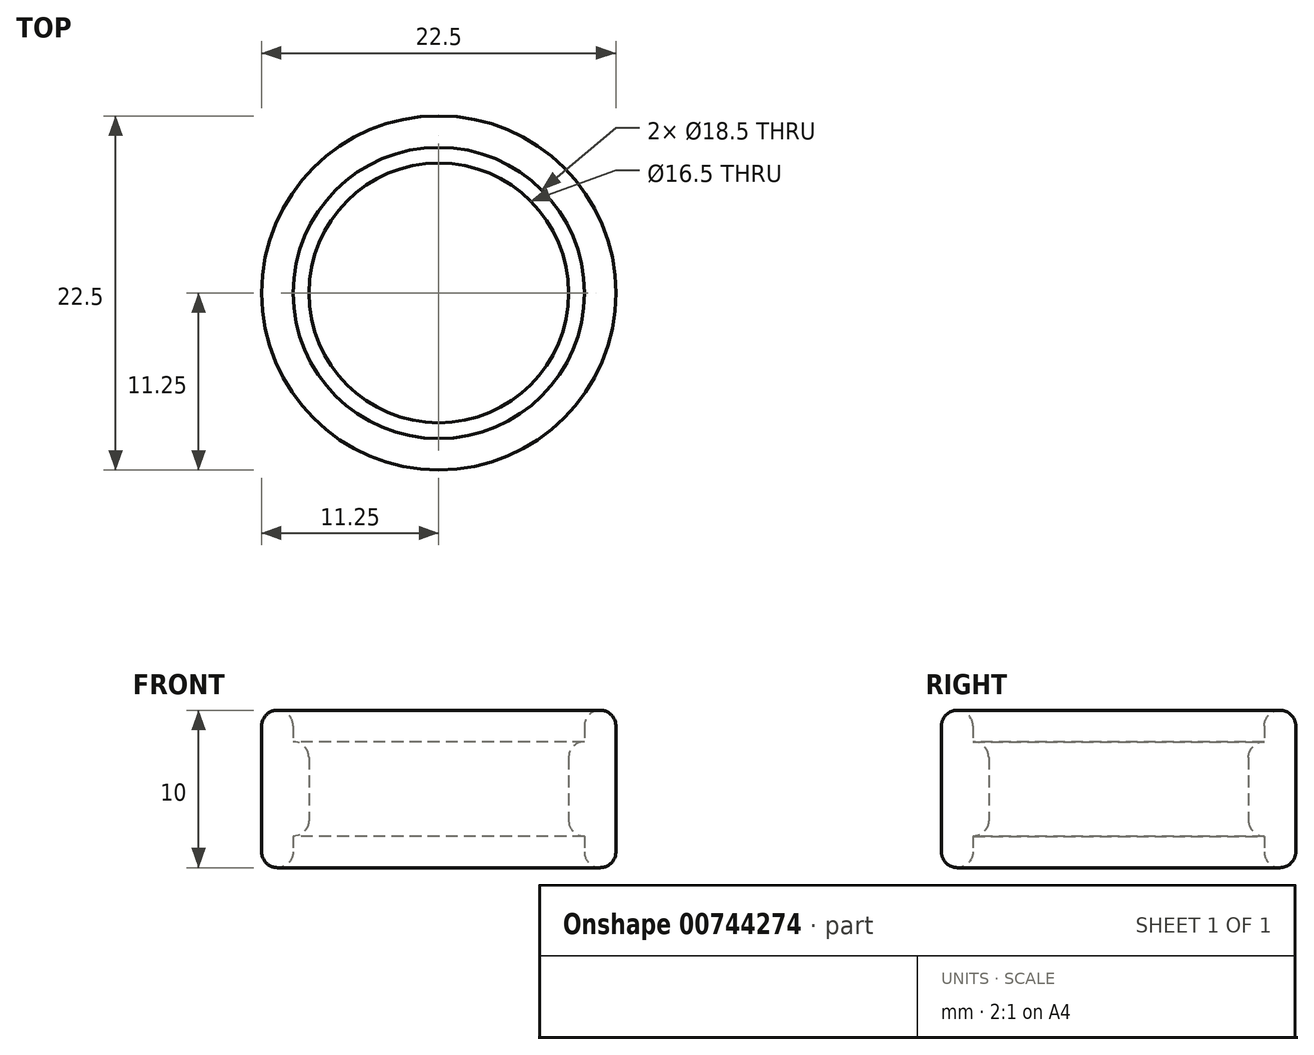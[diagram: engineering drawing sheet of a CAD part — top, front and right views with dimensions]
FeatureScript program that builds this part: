
annotation { "Feature Type Name" : "Feature", "Feature Type Description" : "" }
export const myFeature = defineFeature(function(context is Context, id is Id, definition is map)
    precondition{}
    {
        {
            var Q0;
            Q0=qCreatedBy(makeId("Top.planeOp"),FACE);
            var sketch = newSketch(context, id + "F0", { "sketchPlane" : qUnion([Q0])});
            skCircle(sketch, "E0", {"center": v(0, 0) * mm, "radius": 11.25 * mm});
            skCircle(sketch, "E1", {"center": v(0, 0) * mm, "radius": 9.25 * mm});
            skSolve(sketch);
        }
        {
            var Q0;
            Q0=makeQuery(id+"F0.imprint","IMPRINT",FACE,{"disambiguationData":[TD([[makeQuery(id+"F0.imprint","IMPRINT",EDGE,{"derivedFrom":sQuery(id+"F0.wireOp",EDGE,"E0")}),1.0]])]});
            extrude(context, id + "F1", {"entities" : qUnion([Q0]), "depth" : 10 * mm, "offsetDistance" : 25 * mm});
        }
        {
            var Q0;
            Q0=qCreatedBy(makeId("Top.planeOp"),FACE);
            cPlane(context, id + "F2", {"entities" : qUnion([Q0]), "cplaneType" : CPlaneType.OFFSET, "offset" : 2 * mm, "width" : 150 * mm, "height" : 150 * mm});
        }
        {
            var Q0;
            Q0=qCreatedBy(id+"F2.planeOp",FACE);
            var sketch = newSketch(context, id + "F3", { "sketchPlane" : qUnion([Q0])});
            skCircle(sketch, "E2", {"center": v(0, 0) * mm, "radius": 8.25 * mm});
            skCircle(sketch, "E3", {"center": v(0, 0) * mm, "radius": 11.25 * mm});
            skSolve(sketch);
        }
        {
            var Q0;
            Q0 = qSketchRegion(id + "F3", true);
            extrude(context, id + "F4", {"entities" : qUnion([Q0]), "operationType" : NewBodyOperationType.ADD, "depth" : 6 * mm, "offsetDistance" : 25 * mm});
        }
        {
            var Q0;
            Q0=makeQuery(id+"F4.opExtrude","CAP_EDGE",EDGE,{"disambiguationData":[OSD([sQuery(id+"F3.wireOp",EDGE,"E2")])],"isStart":true});
            var Q1;
            Q1=makeQuery(id+"F4.opExtrude","CAP_EDGE",EDGE,{"disambiguationData":[OSD([sQuery(id+"F3.wireOp",EDGE,"E2")])],"isStart":false});
            var Q2;
            Q2=makeQuery(id+"F1.opExtrude","CAP_EDGE",EDGE,{"disambiguationData":[OSD([sQuery(id+"F0.wireOp",EDGE,"E1")])],"isStart":false});
            var Q3;
            Q3=makeQuery(id+"F1.opExtrude","CAP_EDGE",EDGE,{"disambiguationData":[OSD([sQuery(id+"F0.wireOp",EDGE,"E0")])],"isStart":false});
            var Q4;
            Q4=makeQuery(id+"F1.opExtrude","CAP_EDGE",EDGE,{"disambiguationData":[OSD([sQuery(id+"F0.wireOp",EDGE,"E0")])],"isStart":true});
            var Q5;
            Q5=makeQuery(id+"F1.opExtrude","CAP_EDGE",EDGE,{"disambiguationData":[OSD([sQuery(id+"F0.wireOp",EDGE,"E1")])],"isStart":true});
            fillet(context, id + "F5", {"entities" : qUnion([Q0, Q1, Q2, Q3, Q4, Q5]), "radius" : 1 * mm, "tangentPropagation" : true, "allowEdgeOverflow" : false});
        }
    });
